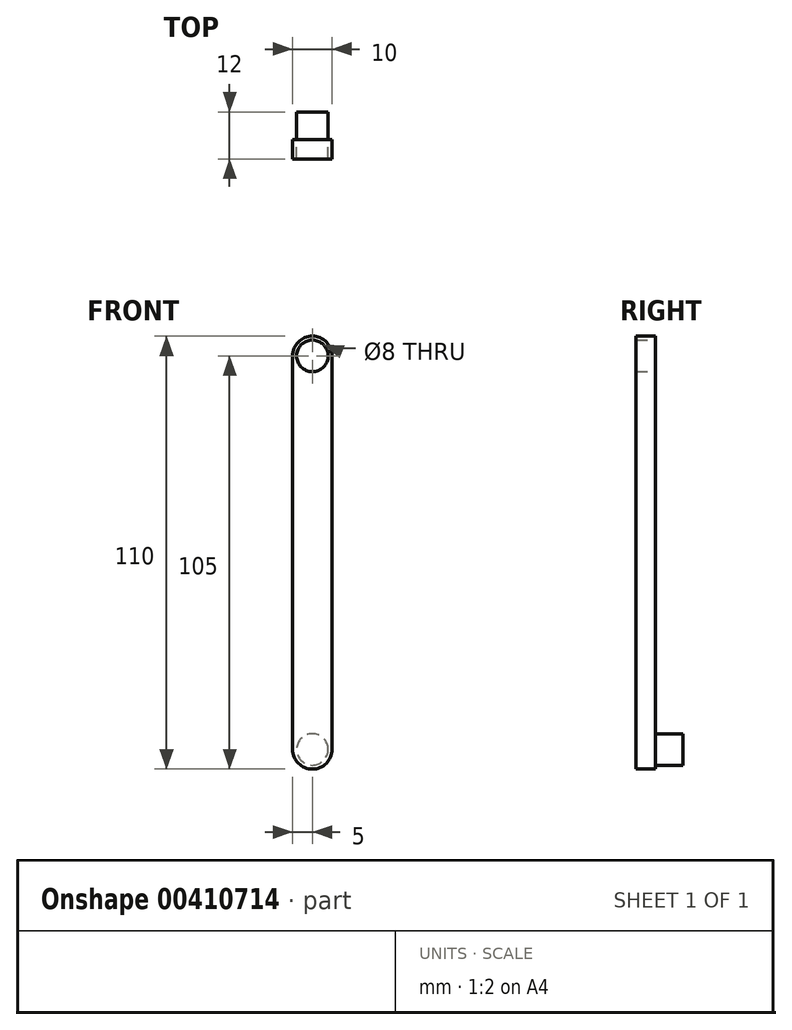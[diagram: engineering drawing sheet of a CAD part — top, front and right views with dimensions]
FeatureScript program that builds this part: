
annotation { "Feature Type Name" : "Feature", "Feature Type Description" : "" }
export const myFeature = defineFeature(function(context is Context, id is Id, definition is map)
    precondition{}
    {
        {
            var Q0;
            Q0=qCreatedBy(makeId("Front.planeOp"),FACE);
            var sketch = newSketch(context, id + "F0", { "sketchPlane" : qUnion([Q0])});
            skLineSegment(sketch, "E0.bottom", {"start": v(0, 0) * mm, "end": v(10, 0) * mm});
            skLineSegment(sketch, "E0.top", {"start": v(0, -100) * mm, "end": v(10, -100) * mm});
            skLineSegment(sketch, "E0.left", {"start": v(0, 0) * mm, "end": v(0, -100) * mm});
            skLineSegment(sketch, "E0.right", {"start": v(10, 0) * mm, "end": v(10, -100) * mm});
            skArc(sketch, "E1", {"start": v(0, 0) * mm, "mid": v(5, 5) * mm, "end": v(10, 0) * mm});
            skArc(sketch, "E2", {"start": v(0, -100) * mm, "mid": v(5, -105) * mm, "end": v(10, -100) * mm});
            skCircle(sketch, "E3", {"center": v(5, -100) * mm, "radius": 5 * mm});
            skCircle(sketch, "E4.0", {"center": v(5, -100) * mm, "radius": 4 * mm});
            skCircle(sketch, "E5", {"center": v(5, 0) * mm, "radius": 5 * mm});
            skCircle(sketch, "E6.0", {"center": v(5, 0) * mm, "radius": 4 * mm});
            skSolve(sketch);
        }
        {
            var Q0;
            Q0 = qSketchRegion(id + "F0", true);
            var Q1;
            {var subQ0=sQuery(id+"F0.wireOp",EDGE,"E4.0");var subQ1=sQuery(id+"F0.wireOp",EDGE,"E0.top");var subQ2=makeQuery(id+"F0.imprint","INTERSECT",VERTEX,{"disambiguationData":[OD(0.0)],"derivedFrom":[subQ1,subQ0]});Q1=makeQuery(id+"F0.imprint","IMPRINT",FACE,{"disambiguationData":[TD([[makeQuery(id+"F0.imprint","IMPRINT",EDGE,{"disambiguationData":[TD([[subQ2,-1.0]])],"derivedFrom":subQ1}),-1.0]])]});}
            var Q2;
            {var subQ0=sQuery(id+"F0.wireOp",EDGE,"E4.0");var subQ1=sQuery(id+"F0.wireOp",EDGE,"E0.top");var subQ2=makeQuery(id+"F0.imprint","INTERSECT",VERTEX,{"disambiguationData":[OD(0.0)],"derivedFrom":[subQ1,subQ0]});Q2=makeQuery(id+"F0.imprint","IMPRINT",FACE,{"disambiguationData":[TD([[makeQuery(id+"F0.imprint","IMPRINT",EDGE,{"disambiguationData":[TD([[subQ2,-1.0]])],"derivedFrom":subQ1}),1.0]])]});}
            extrude(context, id + "F1", {"entities" : qUnion([Q0, Q1, Q2]), "depth" : 5 * mm});
        }
        {
            var Q0;
            {var subQ0=sQuery(id+"F0.wireOp",EDGE,"E4.0");var subQ1=sQuery(id+"F0.wireOp",EDGE,"E0.top");var subQ2=makeQuery(id+"F0.imprint","INTERSECT",VERTEX,{"disambiguationData":[OD(0.0)],"derivedFrom":[subQ1,subQ0]});Q0=makeQuery(id+"F0.imprint","IMPRINT",FACE,{"disambiguationData":[TD([[makeQuery(id+"F0.imprint","IMPRINT",EDGE,{"disambiguationData":[TD([[subQ2,-1.0]])],"derivedFrom":subQ1}),-1.0]])]});}
            var Q1;
            {var subQ0=sQuery(id+"F0.wireOp",EDGE,"E4.0");var subQ1=sQuery(id+"F0.wireOp",EDGE,"E0.top");var subQ2=makeQuery(id+"F0.imprint","INTERSECT",VERTEX,{"disambiguationData":[OD(0.0)],"derivedFrom":[subQ1,subQ0]});Q1=makeQuery(id+"F0.imprint","IMPRINT",FACE,{"disambiguationData":[TD([[makeQuery(id+"F0.imprint","IMPRINT",EDGE,{"disambiguationData":[TD([[subQ2,-1.0]])],"derivedFrom":subQ1}),1.0]])]});}
            extrude(context, id + "F2", {"entities" : qUnion([Q0, Q1]), "operationType" : NewBodyOperationType.ADD, "oppositeDirection" : true, "depth" : 7 * mm});
        }
    });
